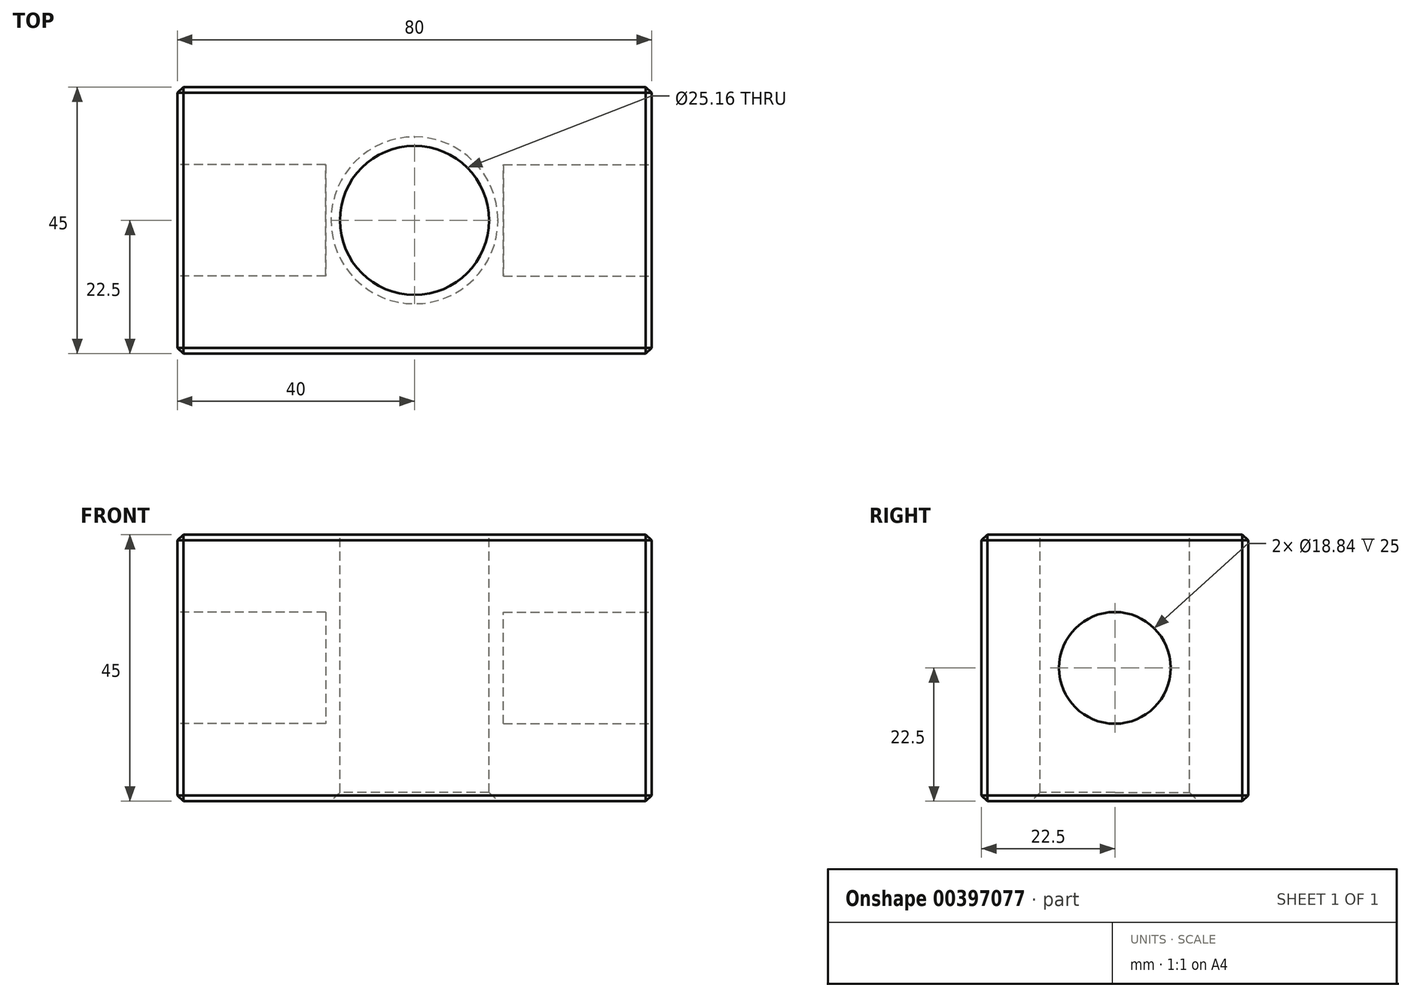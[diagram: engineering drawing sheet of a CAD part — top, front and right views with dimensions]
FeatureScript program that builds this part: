
annotation { "Feature Type Name" : "Feature", "Feature Type Description" : "" }
export const myFeature = defineFeature(function(context is Context, id is Id, definition is map)
    precondition{}
    {
        {
            var Q0;
            Q0=qCreatedBy(makeId("Front.planeOp"),FACE);
            var sketch = newSketch(context, id + "F0", { "sketchPlane" : qUnion([Q0])});
            skLineSegment(sketch, "E0.bottom", {"start": v(40, 22.5) * mm, "end": v(-40, 22.5) * mm});
            skLineSegment(sketch, "E0.top", {"start": v(40, -22.5) * mm, "end": v(-40, -22.5) * mm});
            skLineSegment(sketch, "E0.left", {"start": v(40, 22.5) * mm, "end": v(40, -22.5) * mm});
            skLineSegment(sketch, "E0.right", {"start": v(-40, 22.5) * mm, "end": v(-40, -22.5) * mm});
            skPoint(sketch, "E0.middle", {"position": v(0, 0) * mm});
            skSolve(sketch);
        }
        {
            var Q0;
            Q0 = qSketchRegion(id + "F0", true);
            extrude(context, id + "F1", {"entities" : qUnion([Q0]), "endBound" : BoundingType.SYMMETRIC, "depth" : 45 * mm});
        }
        {
            var Q0;
            Q0=makeQuery(id+"F1.opExtrude","SWEPT_FACE",FACE,{"disambiguationData":[OSD([sQuery(id+"F0.wireOp",EDGE,"E0.bottom")])]});
            var sketch = newSketch(context, id + "F2", { "sketchPlane" : qUnion([Q0])});
            skCircle(sketch, "E1", {"center": v(0, 0) * mm, "radius": 12.58 * mm});
            skSolve(sketch);
        }
        {
            var Q0;
            Q0 = qSketchRegion(id + "F2", true);
            extrude(context, id + "F3", {"entities" : qUnion([Q0]), "operationType" : NewBodyOperationType.REMOVE, "endBound" : BoundingType.THROUGH_ALL, "oppositeDirection" : true, "depth" : 25 * mm});
        }
        {
            var Q0;
            Q0=makeQuery(id+"F1.opExtrude","SWEPT_FACE",FACE,{"disambiguationData":[OSD([sQuery(id+"F0.wireOp",EDGE,"E0.left")])]});
            var sketch = newSketch(context, id + "F4", { "sketchPlane" : qUnion([Q0])});
            skCircle(sketch, "E2", {"center": v(0, 0) * mm, "radius": 9.42 * mm});
            skSolve(sketch);
        }
        {
            var Q0;
            Q0 = qSketchRegion(id + "F4", true);
            extrude(context, id + "F5", {"entities" : qUnion([Q0]), "operationType" : NewBodyOperationType.REMOVE, "oppositeDirection" : true, "depth" : 25 * mm});
        }
        {
            var Q0;
            Q0=makeQuery(id+"F1.opExtrude","SWEPT_FACE",FACE,{"disambiguationData":[OSD([sQuery(id+"F0.wireOp",EDGE,"E0.right")])]});
            var sketch = newSketch(context, id + "F6", { "sketchPlane" : qUnion([Q0])});
            skCircle(sketch, "E3", {"center": v(0, 0) * mm, "radius": 9.42 * mm});
            skSolve(sketch);
        }
        {
            var Q0;
            Q0 = qSketchRegion(id + "F6", true);
            extrude(context, id + "F7", {"entities" : qUnion([Q0]), "operationType" : NewBodyOperationType.REMOVE, "oppositeDirection" : true, "depth" : 25 * mm});
        }
        {
            var Q0;
            Q0=makeQuery(id+"F3.boolean.opBoolean","COPY",EDGE,{"derivedFrom":makeQuery(id+"F3.opExtrude","CAP_EDGE",EDGE,{"disambiguationData":[OSD([sQuery(id+"F2.wireOp",EDGE,"E1")])],"isStart":true})});
            var Q1;
            Q1=makeQuery(id+"F5.boolean.opBoolean","COPY",EDGE,{"derivedFrom":makeQuery(id+"F5.opExtrude","CAP_EDGE",EDGE,{"disambiguationData":[OSD([sQuery(id+"F4.wireOp",EDGE,"E2")])],"isStart":true})});
            var Q2;
            Q2=makeQuery(id+"F3.boolean.opBoolean","INTERSECT",EDGE,{"derivedFrom":[makeQuery(id+"F1.opExtrude","SWEPT_FACE",FACE,{"disambiguationData":[OSD([sQuery(id+"F0.wireOp",EDGE,"E0.top")])]}),makeQuery(id+"F3.opExtrude","SWEPT_FACE",FACE,{"disambiguationData":[OSD([sQuery(id+"F2.wireOp",EDGE,"E1")])]})]});
            var Q3;
            Q3=makeQuery(id+"F7.boolean.opBoolean","COPY",EDGE,{"derivedFrom":makeQuery(id+"F7.opExtrude","CAP_EDGE",EDGE,{"disambiguationData":[OSD([sQuery(id+"F6.wireOp",EDGE,"E3")])],"isStart":true})});
            chamfer(context, id + "F8", {"entities" : qUnion([Q0, Q1, Q2, Q3]), "width" : 1.5 * mm, "tangentPropagation" : true});
        }
        {
            var Q0;
            Q0=makeQuery(id+"F1.opExtrude","CAP_EDGE",EDGE,{"disambiguationData":[OSD([sQuery(id+"F0.wireOp",EDGE,"E0.bottom")])],"isStart":false});
            var Q1;
            Q1=makeQuery(id+"F1.opExtrude","CAP_EDGE",EDGE,{"disambiguationData":[OSD([sQuery(id+"F0.wireOp",EDGE,"E0.left")])],"isStart":false});
            var Q2;
            Q2=makeQuery(id+"F1.opExtrude","CAP_EDGE",EDGE,{"disambiguationData":[OSD([sQuery(id+"F0.wireOp",EDGE,"E0.top")])],"isStart":false});
            var Q3;
            Q3=makeQuery(id+"F1.opExtrude","CAP_EDGE",EDGE,{"disambiguationData":[OSD([sQuery(id+"F0.wireOp",EDGE,"E0.right")])],"isStart":false});
            var Q4;
            Q4=makeQuery(id+"F1.opExtrude","SWEPT_EDGE",EDGE,{"disambiguationData":[OSD([sQuery(id+"F0.wireOp",EDGE,"E0.bottom"),sQuery(id+"F0.wireOp",EDGE,"E0.left")])]});
            var Q5;
            Q5=makeQuery(id+"F1.opExtrude","CAP_EDGE",EDGE,{"disambiguationData":[OSD([sQuery(id+"F0.wireOp",EDGE,"E0.bottom")])],"isStart":true});
            var Q6;
            Q6=makeQuery(id+"F1.opExtrude","SWEPT_EDGE",EDGE,{"disambiguationData":[OSD([sQuery(id+"F0.wireOp",EDGE,"E0.bottom"),sQuery(id+"F0.wireOp",EDGE,"E0.right")])]});
            var Q7;
            Q7=makeQuery(id+"F1.opExtrude","SWEPT_EDGE",EDGE,{"disambiguationData":[OSD([sQuery(id+"F0.wireOp",EDGE,"E0.top"),sQuery(id+"F0.wireOp",EDGE,"E0.left")])]});
            var Q8;
            Q8=makeQuery(id+"F1.opExtrude","CAP_EDGE",EDGE,{"disambiguationData":[OSD([sQuery(id+"F0.wireOp",EDGE,"E0.left")])],"isStart":true});
            var Q9;
            Q9=makeQuery(id+"F1.opExtrude","CAP_EDGE",EDGE,{"disambiguationData":[OSD([sQuery(id+"F0.wireOp",EDGE,"E0.top")])],"isStart":true});
            var Q10;
            Q10=makeQuery(id+"F1.opExtrude","CAP_EDGE",EDGE,{"disambiguationData":[OSD([sQuery(id+"F0.wireOp",EDGE,"E0.right")])],"isStart":true});
            var Q11;
            Q11=makeQuery(id+"F1.opExtrude","SWEPT_EDGE",EDGE,{"disambiguationData":[OSD([sQuery(id+"F0.wireOp",EDGE,"E0.top"),sQuery(id+"F0.wireOp",EDGE,"E0.right")])]});
            chamfer(context, id + "F9", {"entities" : qUnion([Q0, Q1, Q2, Q3, Q4, Q5, Q6, Q7, Q8, Q9, Q10, Q11]), "width" : 1 * mm, "tangentPropagation" : true});
        }
    });
